# Revit family: Air Terminal_11
name_source: partatom
category: Air Terminals
revit_build: Autodesk Revit 2018 (Build: 20180423_1000(x64)
units: mm (PartAtom-declared; Revit-internal decimal feet)

## family parameters
Always vertical = Yes
Cut with Voids When Loaded = No
Part Type = Normal
Room Calculation Point = Yes
Round Connector Dimension = Use Diameter
Shared = No
Work Plane-Based = No

## types (1)
- PTR - TLAK
    Broj resetki = 7
    Cost = 1 $
    Diffuser Width = 0 mm  [stored 0 ft]
    Duct Diameter = 250 mm  [stored 0.82021 ft]
    Duct Height = 100 mm
    Duct Width = 200 mm
    Grille Height = 40 mm  [stored 0.131234 ft]
    Grille Length = 252 mm
    Grille Width = 152 mm
    Length 1 = 13 mm
    Panel Thickness = 5 mm  [stored 0.0164042 ft]
    Sirina lopatice = 1 mm  [stored 0.00328084 ft]
    TP_Efektivna povrsina = 1 m²
    TP_Sirina prikljucka = 225 mm
    TP_Visina prikljucka = 125 mm
    Udaljenost Skice = 17 mm

note: [stored X ft] marks values corroborated as IEEE doubles in the binary element streams (Revit-internal decimal feet)

## geometry (parser evidence)
native form markers: Sweep x3
no freeform markers — native parametric forms only
